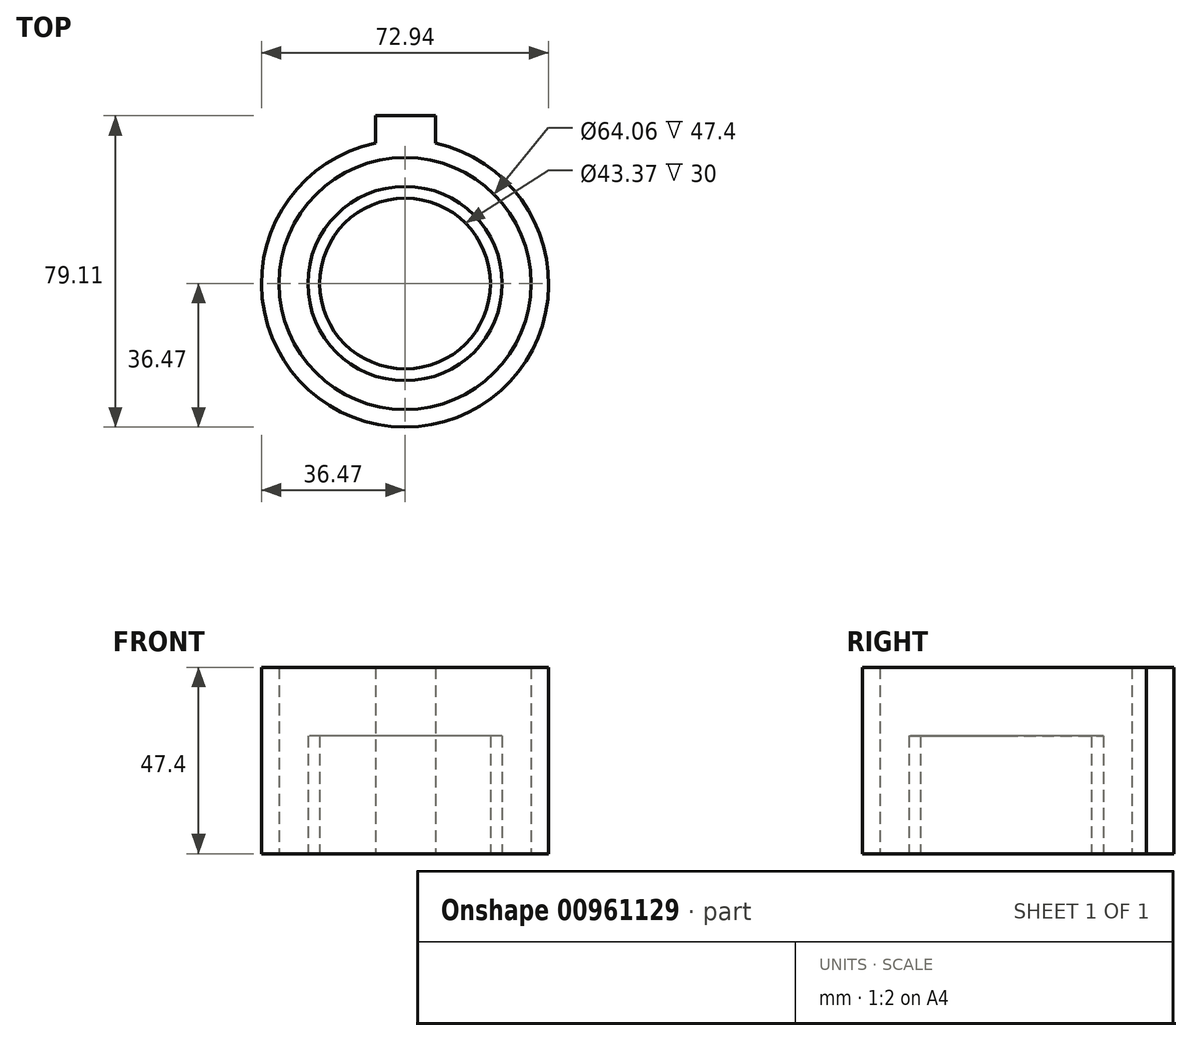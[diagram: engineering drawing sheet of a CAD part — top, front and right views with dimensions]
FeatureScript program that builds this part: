
annotation { "Feature Type Name" : "Feature", "Feature Type Description" : "" }
export const myFeature = defineFeature(function(context is Context, id is Id, definition is map)
    precondition{}
    {
        {
            var Q0;
            Q0=qCreatedBy(makeId("Top.planeOp"),FACE);
            var sketch = newSketch(context, id + "F0", { "sketchPlane" : qUnion([Q0])});
            skCircle(sketch, "E0", {"center": v(0, 0) * mm, "radius": 21.69 * mm});
            skCircle(sketch, "E1.0", {"center": v(0, 0) * mm, "radius": 24.69 * mm});
            skCircle(sketch, "E2", {"center": v(0, 0) * mm, "radius": 32.03 * mm});
            skCircle(sketch, "E3", {"center": v(0, 0) * mm, "radius": 36.47 * mm});
            skLineSegment(sketch, "E4.bottom", {"start": v(-7.56, 42.64) * mm, "end": v(7.74, 42.64) * mm});
            skLineSegment(sketch, "E4.top", {"start": v(-7.56, 35.18) * mm, "end": v(7.74, 35.18) * mm});
            skLineSegment(sketch, "E4.left", {"start": v(-7.56, 42.64) * mm, "end": v(-7.56, 35.18) * mm});
            skLineSegment(sketch, "E4.right", {"start": v(7.74, 42.64) * mm, "end": v(7.74, 35.18) * mm});
            skPoint(sketch, "E5.oppositeSnap0", {"position": v(-7.56, 38.9) * mm});
            skSolve(sketch);
        }
        {
            var Q0;
            Q0=makeQuery(id+"F0.imprint","IMPRINT",FACE,{"disambiguationData":[TD([[makeQuery(id+"F0.imprint","IMPRINT",EDGE,{"derivedFrom":sQuery(id+"F0.wireOp",EDGE,"E0")}),-1.0]])]});
            extrude(context, id + "F1", {"entities" : qUnion([Q0]), "depth" : 30 * mm, "offsetDistance" : 25 * mm});
        }
        {
            var Q0;
            Q0 = qSketchRegion(id + "F0", true);
            extrude(context, id + "F2", {"entities" : qUnion([Q0]), "depth" : 47.4 * mm, "offsetDistance" : 25 * mm});
        }
    });
